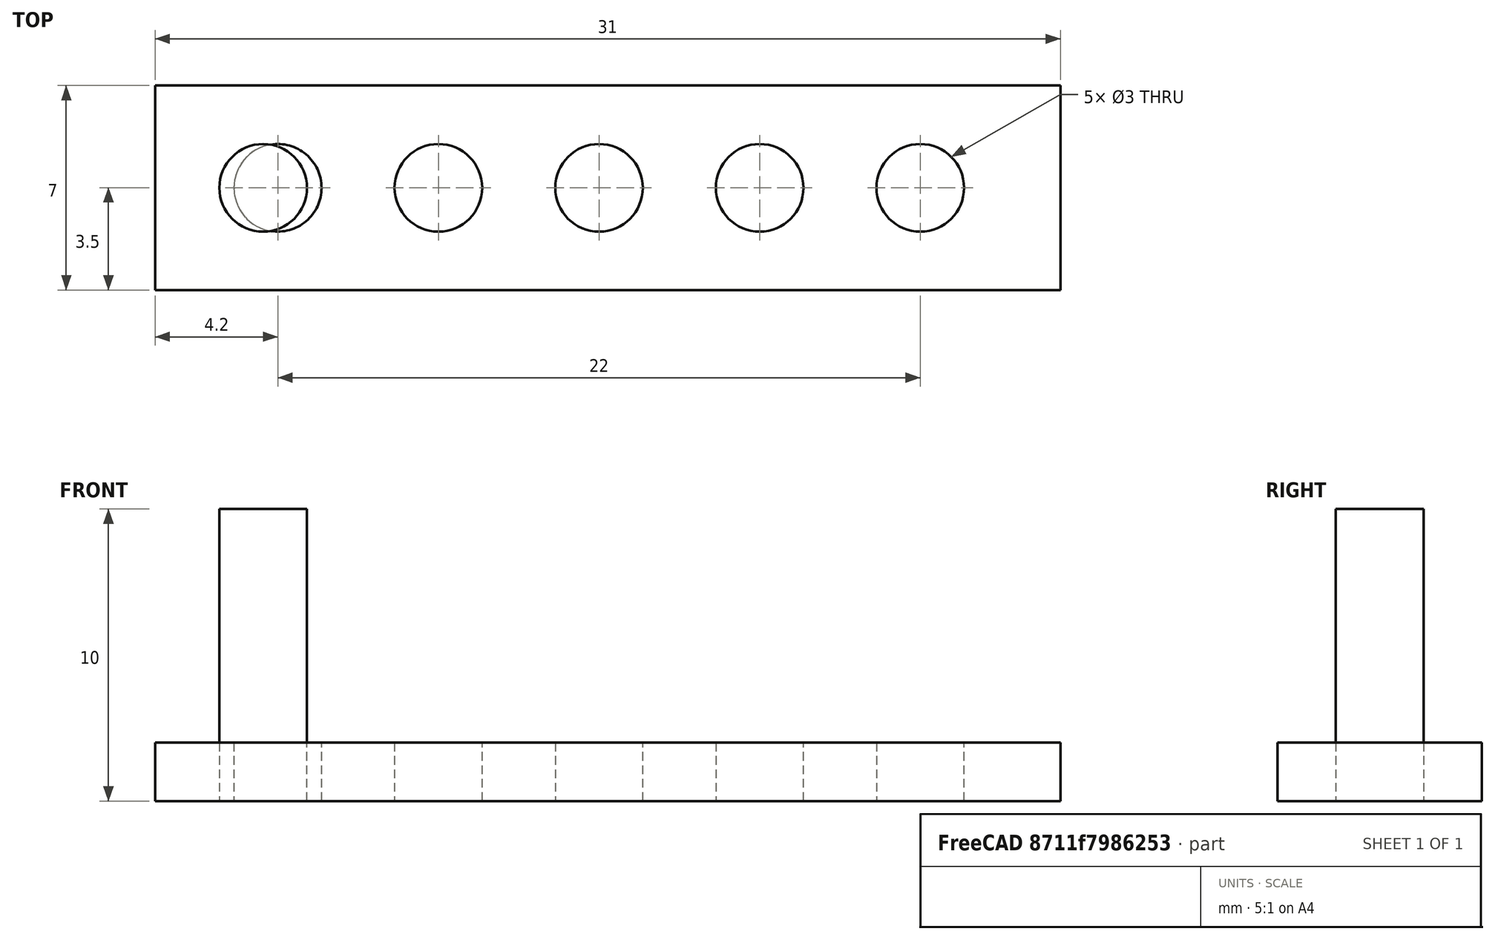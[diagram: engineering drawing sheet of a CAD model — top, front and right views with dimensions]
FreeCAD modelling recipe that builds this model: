
FCSTD DOCUMENT  (FreeCAD 1.0R39319 (Git))
Label: ojt1_t10r01_array_cylinder
License: All rights reserved
LicenseURL: https://en.wikipedia.org/wiki/All_rights_reserved
objects: Part::Cylinder×1, Part::Box×1, Part::FeaturePython×1, Part::Cut×1
note: 3 computed .brp shape members not serialized (recipe doc carries the construction recipe); baked Part::Feature solids carry a one-line shape summary decoded from their .brp

FEATURE [Part::Cylinder] Cylinder  label="Cilindre"
  Angle = 360
  AttacherType = Attacher::AttachEngine3D
  FirstAngle = 0
  Height = 10
  Placement = pos=(3.7,3.5,0) rot=(0,0,1;0rad)
  Radius = 1.5
  SecondAngle = 0
FEATURE [Part::Box] Box  label="Cub"
  AttacherType = Attacher::AttachEngine3D
  Height = 2
  Length = 31
  Width = 7
FEATURE [Part::FeaturePython] Array  # Draft array (typed FeaturePython)
  AlwaysSyncPlacement = false
  Angle = 360
  ArrayType = 0
  Axis = (0,0,1)
  Base = -> Cylinder
  Center = (0,0,0)
  Count = 5
  ExpandArray = false
  Fuse = false
  IntervalAxis = (0,0,0)
  IntervalX = (5.5,0,0)
  IntervalY = (0,10,0)
  IntervalZ = (0,0,100)
  NumberCircles = 3
  NumberPolar = 5
  NumberX = 5
  NumberY = 0
  NumberZ = 0
  Placement = pos=(0.5,0,0) rot=(0,0,1;0rad)
  PlacementList = 5 placements: arithmetic series from (3.7,3.5,0) step (5.5,0,0) to (25.7,3.5,0)
  RadialDistance = 50
  ScaleList = (5) [(1,1,1),(1,1,1),(1,1,1),(1,1,1),(1,1,1)]
  Symmetry = 1
  TangentialDistance = 25
FEATURE [Part::Cut] Cut
  Base = -> Box
  Refine = true
  Tool = -> Array
